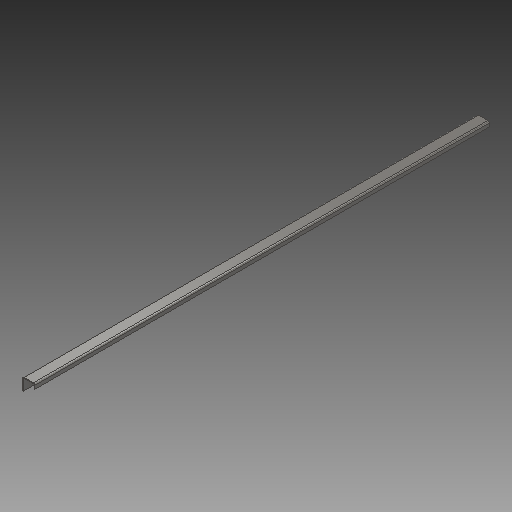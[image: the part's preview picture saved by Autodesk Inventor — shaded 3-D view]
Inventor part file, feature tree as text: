
AUTODESK INVENTOR PART (.ipt)
format: ipt  version: 2017 (Build 210142000, 142)  size: 142,336 bytes
history: native  units: mm
features: sheet_metal_op x3, other x2, sketch x1
ambient origin geometry x8: Origin, YZ Plane, XZ Plane, XY Plane, X Axis, Y Axis, Z Axis, Center Point
bodies: Solid1 (feature_tree)
feature tree (6):
  sheet_metal_op  "Contour Flange1"
  sketch  "Sketch1"  dims[d0=25.0mm d1=25.0mm d2=10.0mm d3=1.5mm d4=0.75mm d5=3.0mm d6=1.5mm d7=930.0mm d8=1.5mm d9=0.5mm d10=6.0mm d11=1.5mm d12=1.5mm]
  other  "Plate1"
  sheet_metal_op  "Bend1"
  sheet_metal_op  "Corner1"
  other  "Definition1"
